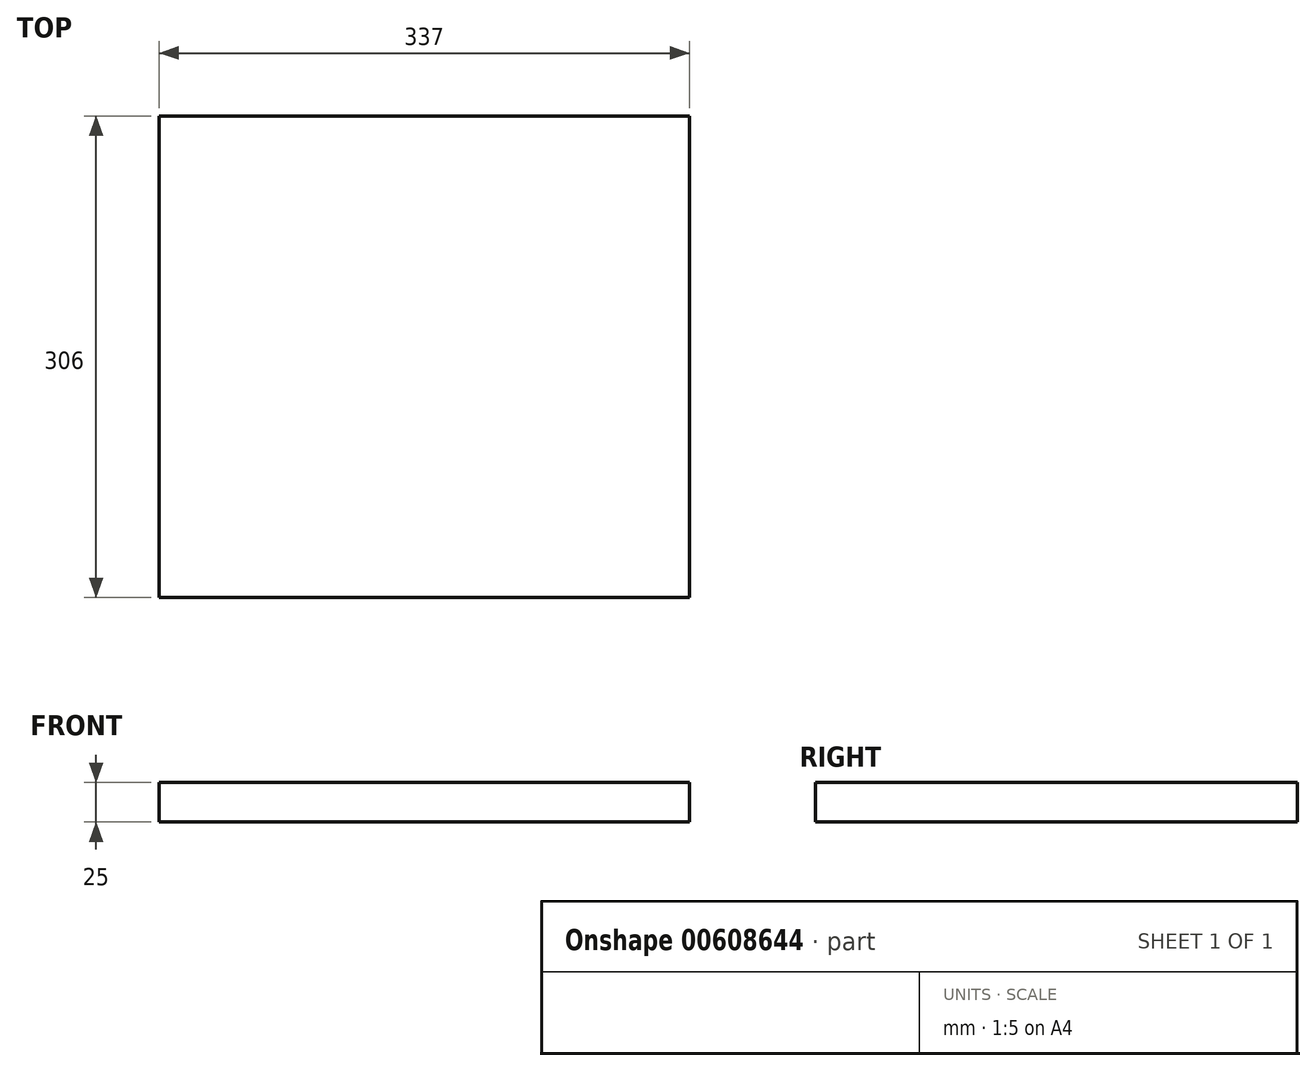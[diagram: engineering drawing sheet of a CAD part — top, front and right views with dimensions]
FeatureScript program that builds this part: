
annotation { "Feature Type Name" : "Feature", "Feature Type Description" : "" }
export const myFeature = defineFeature(function(context is Context, id is Id, definition is map)
    precondition{}
    {
        {
            var Q0;
            Q0=qCreatedBy(makeId("Top.planeOp"),FACE);
            var sketch = newSketch(context, id + "F0", { "sketchPlane" : qUnion([Q0])});
            skLineSegment(sketch, "E0.bottom", {"start": v(168.5, 153) * mm, "end": v(-168.5, 153) * mm});
            skLineSegment(sketch, "E0.top", {"start": v(168.5, -153) * mm, "end": v(-168.5, -153) * mm});
            skLineSegment(sketch, "E0.left", {"start": v(168.5, 153) * mm, "end": v(168.5, -153) * mm});
            skLineSegment(sketch, "E0.right", {"start": v(-168.5, 153) * mm, "end": v(-168.5, -153) * mm});
            skPoint(sketch, "E0.middle", {"position": v(0, 0) * mm});
            skSolve(sketch);
        }
        {
            var Q0;
            Q0=makeQuery(id+"F0.imprint","IMPRINT",FACE,{"disambiguationData":[TD([[makeQuery(id+"F0.imprint","IMPRINT",EDGE,{"derivedFrom":sQuery(id+"F0.wireOp",EDGE,"E0.bottom")}),1.0]])]});
            extrude(context, id + "F1", {"entities" : qUnion([Q0]), "depth" : 25 * mm, "offsetDistance" : 25 * mm});
        }
    });
